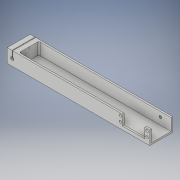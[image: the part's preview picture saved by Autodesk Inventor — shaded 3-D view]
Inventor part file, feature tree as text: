
AUTODESK INVENTOR PART (.ipt)
format: ipt  version: 2017 (Build 210142000, 142)  size: 248,320 bytes
history: native  units: in
note: dims shown in document units (in); Inventor stores cm internally (conversion verified against a paired STEP export)
features: sketch x6, projected_geometry x5, extrude x4, hole x3, fillet x1
ambient origin geometry x8: Origin, YZ Plane, XZ Plane, XY Plane, X Axis, Y Axis, Z Axis, Center Point
bodies: Solid1 (feature_tree)
feature tree (19):
  extrude  "Extrusion1"  Depth=1.685in
  extrude  "Extrusion2"  Depth=1.435in
  extrude  "Extrusion4"  Depth=0.125in TaperAngle=0.0deg
  extrude  "Extrusion5"  Depth=1.0in
  hole  "Hole1"  [1 undecoded]
  hole  "Hole2"  [1 undecoded]
  fillet  "Fillet1"  Radius=0.164in
  hole  "Hole3"  [1 undecoded]
  sketch  "Sketch1"  dims[d0=1.0in d1=1.685in]
  sketch  "Sketch2"  dims[d2=0.875in d3=1.435in]
  projected_geometry  "Projected Loop1"
  projected_geometry  "Projected Loop2"
  sketch  "Sketch4"  dims[d4=0.125in d5=10.436in d6=0.0in]
  projected_geometry  "Projected Loop3"
  sketch  "Sketch5"  dims[d7=0.35in d8=1.0in]
  sketch  "Sketch6"  dims[d9=0.75in d10=2.0in]
  projected_geometry  "Projected Loop4"
  sketch  "Sketch7"  dims[d11=0.19in d12=0.19in d13=0.164in d14=0.3937in d15=0.19in d16=0.19in d19=0.5in d20=0.0in d22=0.776in d23=0.361in d26=0.75in d27=0.133in d28=0.078in d29=0.078in d30=0.098in d31=0.236in d32=0.0665in d33=0.0665in d34=0.0665in d35=0.0in d36=0.118in d37=0.133in d38=1.0in d39=0.5in d40=0.375in d41=0.05in d42=0.35in d43=1.685in d44=0.0in d45=0.75in d46=0.078in d47=0.078in d48=0.098in d49=0.0665in d50=0.0665in d51=0.0665in d52=0.0in d53=0.133in d54=1.0in d55=0.5in d56=0.375in d57=0.35in d58=0.133in d59=0.05in d60=1.685in d61=0.0in d62=0.1in d63=0.1in d64=1.685in d65=0.1in d66=0.8425in d67=0.2106in d68=0.2106in d69=0.158in d70=0.75in d71=0.375in d72=0.25in d73=0.5635in d74=0.355in d75=0.8108in d76=0.104in d77=0.276in d78=0.375in d79=0.25in d80=0.5635in d81=0.432in d82=0.8108in d83=0.125in d84=0.196in d85=0.5in d86=0.375in d87=0.25in d88=0.5635in d89=0.75in d90=0.8108in d91=1.9488in d92=1.9488in d93=0.164in d95=0.3937in d96=0.197in d97=0.197in]
  projected_geometry  "Projected Loop5"
note: 3 required parameter values undecoded (feature->parameter linkage not recoverable at this tier; creation-order binding heuristic only, values carry confidence <= 0.55)
